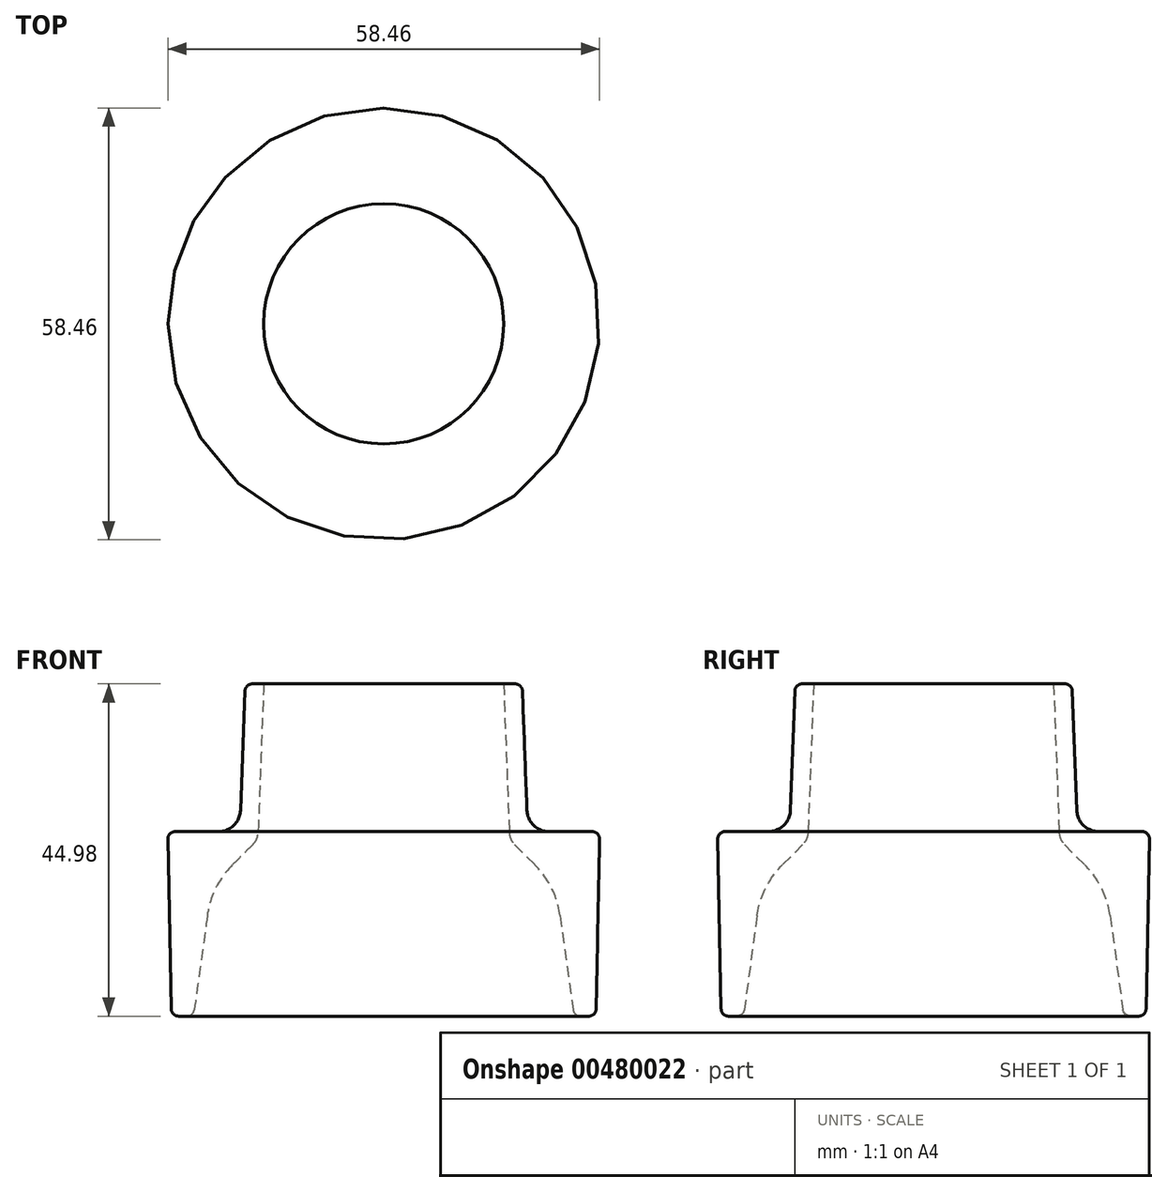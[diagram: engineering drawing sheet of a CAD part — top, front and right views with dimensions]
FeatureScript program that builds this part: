
annotation { "Feature Type Name" : "Feature", "Feature Type Description" : "" }
export const myFeature = defineFeature(function(context is Context, id is Id, definition is map)
    precondition{}
    {
        {
            var Q0;
            Q0=qCreatedBy(makeId("Top.planeOp"),FACE);
            var sketch = newSketch(context, id + "F0", { "sketchPlane" : qUnion([Q0])});
            skCircle(sketch, "E0", {"center": v(0, 0) * mm, "radius": 28.75 * mm});
            skSolve(sketch);
        }
        {
            var Q0;
            Q0=qCreatedBy(makeId("Front.planeOp"),FACE);
            var sketch = newSketch(context, id + "F1", { "sketchPlane" : qUnion([Q0])});
            skLineSegment(sketch, "E1", {"start": v(-28.75, 0) * mm, "end": v(-29.25, 25) * mm});
            skLineSegment(sketch, "E2", {"start": v(-19.5, 25) * mm, "end": v(-29.25, 25) * mm});
            skLineSegment(sketch, "E3", {"start": v(-19.5, 25) * mm, "end": v(-18.75, 45) * mm});
            skLineSegment(sketch, "E4", {"start": v(-28.75, 0) * mm, "end": v(-25.75, 0.06) * mm});
            skArc(sketch, "E5", {"start": v(-17.73, 23.23) * mm, "mid": v(-17.2, 24) * mm, "end": v(-17, 24.9) * mm});
            skLineSegment(sketch, "E6", {"start": v(-17, 24.9) * mm, "end": v(-16.25, 45) * mm});
            skLineSegment(sketch, "E7", {"start": v(-18.75, 45) * mm, "end": v(-16.25, 45) * mm});
            skLineSegment(sketch, "E8", {"start": v(-17.73, 23.23) * mm, "end": v(-20.48, 20.5) * mm});
            skArc(sketch, "E9", {"start": v(-20.48, 20.5) * mm, "mid": v(-22.75, 17.34) * mm, "end": v(-23.89, 13.63) * mm});
            skLineSegment(sketch, "E10", {"start": v(-25.75, 0.06) * mm, "end": v(-23.89, 13.63) * mm});
            skLineSegment(sketch, "E11", {"start": v(0, 0) * mm, "end": v(0, 74.9) * mm, "construction": true});
            skSolve(sketch);
        }
        {
            var Q0;
            Q0 = qSketchRegion(id + "F1", true);
            var Q1;
            Q1=sQuery(id+"F1.wireOp",EDGE,"E11");
            revolve(context, id + "F2", {"entities" : qUnion([Q0]), "axis" : qUnion([Q1]), "revolveType" : RevolveType.FULL});
        }
        {
            var Q0;
            Q0=makeQuery(id+"F2.opRevolve","SWEPT_EDGE",EDGE,{"disambiguationData":[OSD([sQuery(id+"F1.wireOp",EDGE,"E2"),sQuery(id+"F1.wireOp",EDGE,"E3")])]});
            fillet(context, id + "F3", {"entities" : qUnion([Q0]), "radius" : 3 * mm, "tangentPropagation" : true, "allowEdgeOverflow" : false});
        }
        {
            var Q0;
            Q0=makeQuery(id+"F2.opRevolve","SWEPT_EDGE",EDGE,{"disambiguationData":[OSD([sQuery(id+"F1.wireOp",EDGE,"E1"),sQuery(id+"F1.wireOp",EDGE,"E2")])]});
            var Q1;
            Q1=makeQuery(id+"F2.opRevolve","SWEPT_EDGE",EDGE,{"disambiguationData":[OSD([sQuery(id+"F1.wireOp",EDGE,"E3"),sQuery(id+"F1.wireOp",EDGE,"E7")])]});
            var Q2;
            Q2=makeQuery(id+"F2.opRevolve","SWEPT_EDGE",EDGE,{"disambiguationData":[OSD([sQuery(id+"F1.wireOp",EDGE,"E1"),sQuery(id+"F1.wireOp",EDGE,"E4")])]});
            var Q3;
            Q3=makeQuery(id+"F2.opRevolve","SWEPT_EDGE",EDGE,{"disambiguationData":[OSD([sQuery(id+"F1.wireOp",EDGE,"E4"),sQuery(id+"F1.wireOp",EDGE,"E10")])]});
            fillet(context, id + "F4", {"entities" : qUnion([Q0, Q1, Q2, Q3]), "radius" : 1 * mm, "tangentPropagation" : true, "allowEdgeOverflow" : false});
        }
    });
